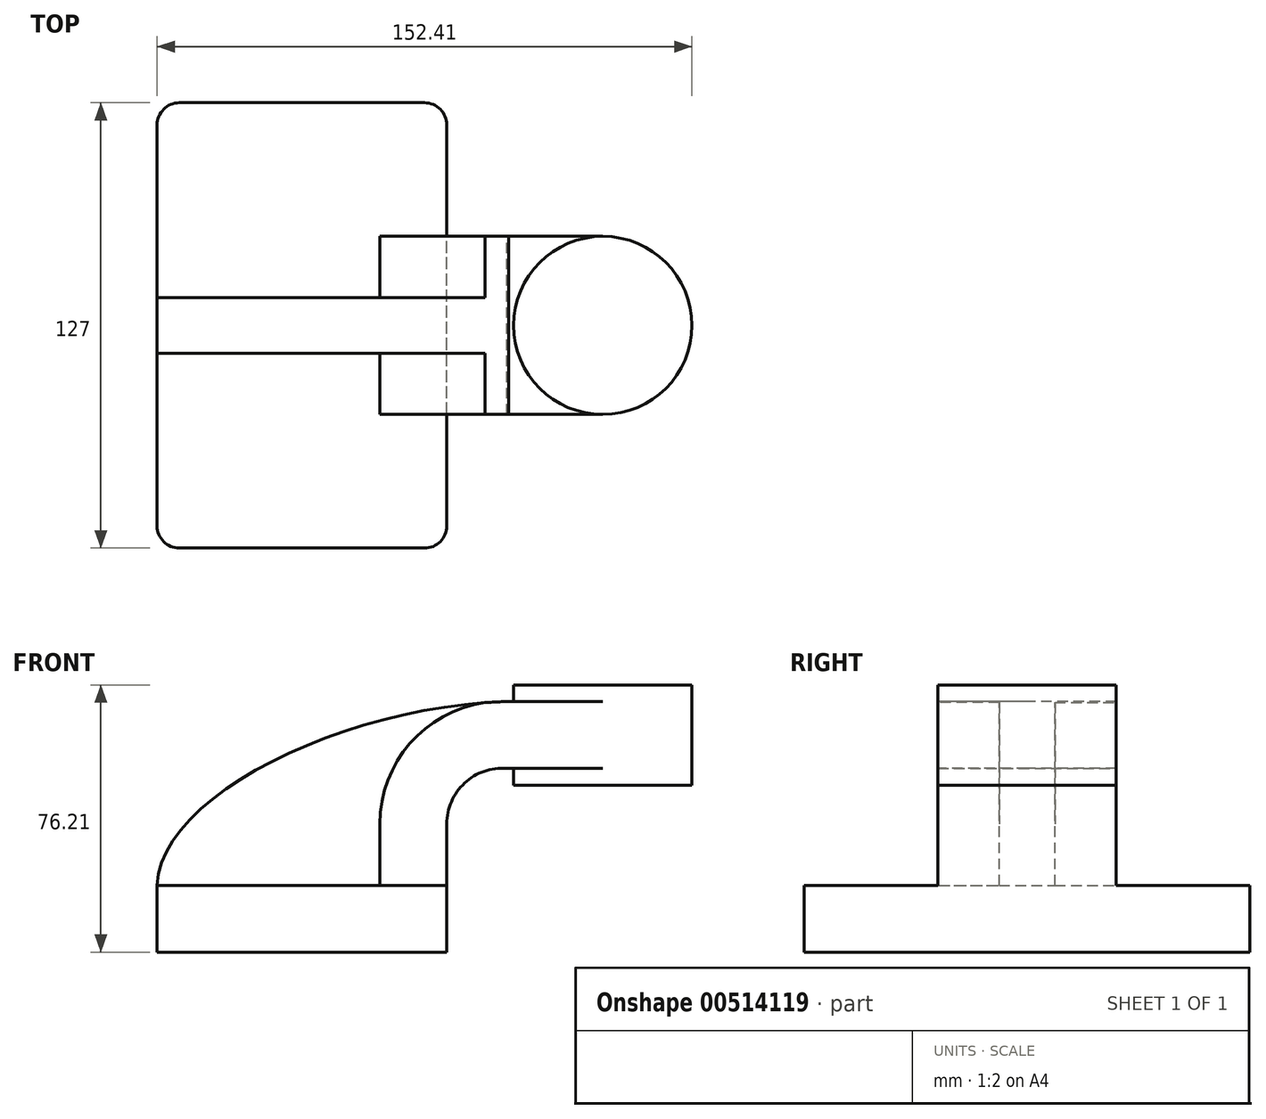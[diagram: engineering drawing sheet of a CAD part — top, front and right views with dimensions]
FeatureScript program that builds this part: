
annotation { "Feature Type Name" : "Feature", "Feature Type Description" : "" }
export const myFeature = defineFeature(function(context is Context, id is Id, definition is map)
    precondition{}
    {
        {
            var Q0;
            Q0=qCreatedBy(makeId("Front.planeOp"),FACE);
            var sketch = newSketch(context, id + "F0", { "sketchPlane" : qUnion([Q0])});
            skLineSegment(sketch, "E0.bottom", {"start": v(-41.28, 9.52) * mm, "end": v(41.28, 9.52) * mm});
            skLineSegment(sketch, "E0.top", {"start": v(-41.28, -9.52) * mm, "end": v(41.28, -9.52) * mm});
            skLineSegment(sketch, "E0.left", {"start": v(-41.28, 9.52) * mm, "end": v(-41.28, -9.52) * mm});
            skLineSegment(sketch, "E0.right", {"start": v(41.28, 9.52) * mm, "end": v(41.28, -9.52) * mm});
            skPoint(sketch, "E0.middle", {"position": v(0, 0) * mm});
            skLineSegment(sketch, "E1.bottom", {"start": v(60.33, 66.68) * mm, "end": v(111.13, 66.68) * mm});
            skLineSegment(sketch, "E1.top", {"start": v(60.33, 38.1) * mm, "end": v(111.13, 38.1) * mm});
            skLineSegment(sketch, "E1.left", {"start": v(60.33, 66.68) * mm, "end": v(60.33, 38.1) * mm});
            skLineSegment(sketch, "E1.right", {"start": v(111.13, 66.68) * mm, "end": v(111.13, 38.1) * mm});
            skPoint(sketch, "E1.middle", {"position": v(85.73, 52.39) * mm});
            skLineSegment(sketch, "E2", {"start": v(41.28, 9.52) * mm, "end": v(41.28, 27.04) * mm});
            skArc(sketch, "E3", {"start": v(41.28, 27.04) * mm, "mid": v(46.35, 38.68) * mm, "end": v(58.33, 42.88) * mm});
            skLineSegment(sketch, "E4", {"start": v(58.33, 42.88) * mm, "end": v(85.73, 42.88) * mm});
            skPoint(sketch, "E5", {"position": v(85.73, 38.1) * mm});
            skLineSegment(sketch, "E6.0", {"start": v(58.9, 61.93) * mm, "end": v(85.73, 61.93) * mm});
            skArc(sketch, "E6.1", {"start": v(22.23, 27.04) * mm, "mid": v(33.08, 52.35) * mm, "end": v(58.9, 61.93) * mm});
            skLineSegment(sketch, "E6.2", {"start": v(22.23, 9.52) * mm, "end": v(22.23, 27.04) * mm});
            skLineSegment(sketch, "E7", {"start": v(85.73, 38.1) * mm, "end": v(85.73, 66.68) * mm});
            skFitSpline(sketch, "E8", {"points": [v(-41.28, 9.52) * mm, v(58.9, 61.93) * mm], "startDerivative": vector(2.53, 77.15) * mm, "endDerivative": vector(138.46, 2.91) * mm});
            skSolve(sketch);
        }
        {
            var Q0;
            Q0=makeQuery(id+"F0.imprint","IMPRINT",FACE,{"disambiguationData":[TD([[makeQuery(id+"F0.imprint","IMPRINT",EDGE,{"derivedFrom":sQuery(id+"F0.wireOp",EDGE,"E0.top")}),1.0]])]});
            extrude(context, id + "F1", {"entities" : qUnion([Q0]), "endBound" : BoundingType.SYMMETRIC, "depth" : 127 * mm});
        }
        {
            var Q0;
            {var subQ1=sQuery(id+"F0.wireOp",EDGE,"E2");Q0=makeQuery(id+"F0.imprint","IMPRINT",FACE,{"disambiguationData":[TD([[makeQuery(id+"F0.imprint","IMPRINT",EDGE,{"derivedFrom":subQ1}),1.0]])]});}
            var Q1;
            {var subQ0=sQuery(id+"F0.wireOp",EDGE,"E6.0");var subQ1=sQuery(id+"F0.wireOp",EDGE,"E1.left");var subQ2=makeQuery(id+"F0.imprint","INTERSECT",VERTEX,{"derivedFrom":[subQ1,subQ0]});Q1=makeQuery(id+"F0.imprint","IMPRINT",FACE,{"disambiguationData":[TD([[makeQuery(id+"F0.imprint","IMPRINT",EDGE,{"disambiguationData":[TD([[subQ2,-1.0]])],"derivedFrom":subQ1}),1.0]])]});}
            extrude(context, id + "F2", {"entities" : qUnion([Q0, Q1]), "operationType" : NewBodyOperationType.ADD, "endBound" : BoundingType.SYMMETRIC, "depth" : 50.8 * mm});
        }
        {
            var Q0;
            {var subQ3=sQuery(id+"F0.wireOp",EDGE,"E6.2");Q0=makeQuery(id+"F0.imprint","IMPRINT",FACE,{"disambiguationData":[TD([[makeQuery(id+"F0.imprint","IMPRINT",EDGE,{"derivedFrom":subQ3}),1.0]])]});}
            extrude(context, id + "F3", {"entities" : qUnion([Q0]), "operationType" : NewBodyOperationType.ADD, "endBound" : BoundingType.SYMMETRIC, "depth" : 15.88 * mm});
        }
        {
            var Q0;
            {var subQ4=sQuery(id+"F0.wireOp",EDGE,"E1.right");Q0=makeQuery(id+"F0.imprint","IMPRINT",FACE,{"disambiguationData":[TD([[makeQuery(id+"F0.imprint","IMPRINT",EDGE,{"derivedFrom":subQ4}),-1.0]])]});}
            var Q1;
            Q1=sQuery(id+"F0.wireOp",EDGE,"E7");
            revolve(context, id + "F4", {"operationType" : NewBodyOperationType.ADD, "entities" : qUnion([Q0]), "axis" : qUnion([Q1]), "revolveType" : RevolveType.FULL});
        }
        {
            var Q0;
            Q0=makeQuery(id+"F1.opExtrude","CAP_EDGE",EDGE,{"disambiguationData":[OSD([sQuery(id+"F0.wireOp",EDGE,"E0.left")])],"isStart":false});
            var Q1;
            Q1=makeQuery(id+"F1.opExtrude","CAP_EDGE",EDGE,{"disambiguationData":[OSD([sQuery(id+"F0.wireOp",EDGE,"E0.right")])],"isStart":false});
            var Q2;
            Q2=makeQuery(id+"F1.opExtrude","CAP_EDGE",EDGE,{"disambiguationData":[OSD([sQuery(id+"F0.wireOp",EDGE,"E0.right")])],"isStart":true});
            var Q3;
            Q3=makeQuery(id+"F1.opExtrude","CAP_EDGE",EDGE,{"disambiguationData":[OSD([sQuery(id+"F0.wireOp",EDGE,"E0.left")])],"isStart":true});
            fillet(context, id + "F5", {"entities" : qUnion([Q0, Q1, Q2, Q3]), "radius" : 6.35 * mm, "tangentPropagation" : true, "allowEdgeOverflow" : false});
        }
    });
